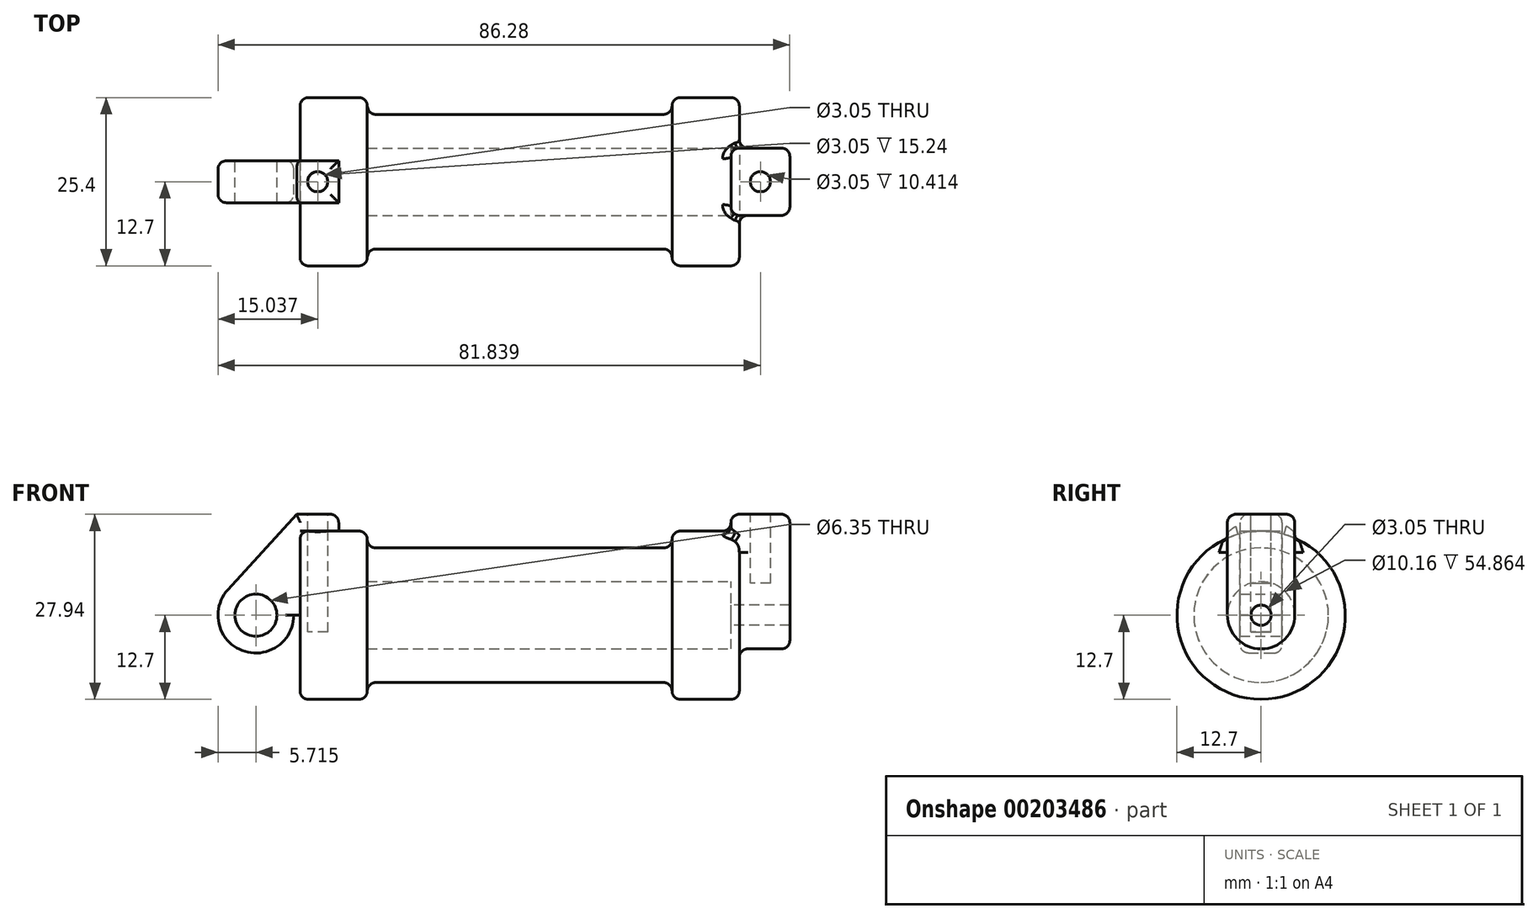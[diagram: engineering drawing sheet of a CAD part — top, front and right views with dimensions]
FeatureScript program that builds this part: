
annotation { "Feature Type Name" : "Feature", "Feature Type Description" : "" }
export const myFeature = defineFeature(function(context is Context, id is Id, definition is map)
    precondition{}
    {
        {
            var Q0;
            Q0=qCreatedBy(makeId("Front.planeOp"),FACE);
            var sketch = newSketch(context, id + "F0", { "sketchPlane" : qUnion([Q0])});
            skLineSegment(sketch, "E0", {"start": v(0, 0) * mm, "end": v(0, 12.7) * mm});
            skLineSegment(sketch, "E1", {"start": v(0, 12.7) * mm, "end": v(10.16, 12.7) * mm});
            skLineSegment(sketch, "E2", {"start": v(10.16, 12.7) * mm, "end": v(10.16, 10.16) * mm});
            skLineSegment(sketch, "E3", {"start": v(10.16, 10.16) * mm, "end": v(56.13, 10.16) * mm});
            skLineSegment(sketch, "E4", {"start": v(56.13, 10.16) * mm, "end": v(56.13, 12.7) * mm});
            skLineSegment(sketch, "E5", {"start": v(56.13, 12.7) * mm, "end": v(66.3, 12.7) * mm});
            skLineSegment(sketch, "E6", {"start": v(66.3, 12.7) * mm, "end": v(66.3, 0) * mm});
            skLineSegment(sketch, "E7", {"start": v(66.3, 0) * mm, "end": v(0, 0) * mm});
            skLineSegment(sketch, "E8", {"start": v(5.84, 15.24) * mm, "end": v(-0.5, 15.24) * mm});
            skLineSegment(sketch, "E9", {"start": v(-0.5, 15.24) * mm, "end": v(-10.88, 3.85) * mm});
            skLineSegment(sketch, "E10", {"start": v(0, 0) * mm, "end": v(-6.65, 0) * mm});
            skCircle(sketch, "E11", {"center": v(-6.65, 0) * mm, "radius": 5.72 * mm});
            skCircle(sketch, "E12", {"center": v(-6.65, 0) * mm, "radius": 3.18 * mm});
            skLineSegment(sketch, "E13", {"start": v(5.84, 15.24) * mm, "end": v(5.84, -9.4) * mm});
            skLineSegment(sketch, "E14", {"start": v(5.84, -9.4) * mm, "end": v(-8.18, -5.5) * mm});
            skSolve(sketch);
        }
        {
            var Q0;
            {var subQ0=sQuery(id+"F0.wireOp",EDGE,"E0");Q0=makeQuery(id+"F0.imprint","IMPRINT",FACE,{"disambiguationData":[TD([[makeQuery(id+"F0.imprint","IMPRINT",EDGE,{"derivedFrom":subQ0}),-1.0]])]});}
            var Q1;
            {var subQ0=sQuery(id+"F0.wireOp",EDGE,"E2");Q1=makeQuery(id+"F0.imprint","IMPRINT",FACE,{"disambiguationData":[TD([[makeQuery(id+"F0.imprint","IMPRINT",EDGE,{"derivedFrom":subQ0}),-1.0]])]});}
            var Q2;
            Q2=sQuery(id+"F0.wireOp",EDGE,"E7");
            revolve(context, id + "F1", {"entities" : qUnion([Q0, Q1]), "axis" : qUnion([Q2]), "revolveType" : RevolveType.FULL});
        }
        {
            var Q0;
            {var subQ3=sQuery(id+"F0.wireOp",EDGE,"E0");Q0=makeQuery(id+"F0.imprint","IMPRINT",FACE,{"disambiguationData":[TD([[makeQuery(id+"F0.imprint","IMPRINT",EDGE,{"derivedFrom":subQ3}),1.0]])]});}
            var Q1;
            {var subQ4=sQuery(id+"F0.wireOp",EDGE,"E12");Q1=makeQuery(id+"F0.imprint","IMPRINT",FACE,{"disambiguationData":[TD([[makeQuery(id+"F0.imprint","IMPRINT",EDGE,{"derivedFrom":subQ4}),-1.0]])]});}
            extrude(context, id + "F2", {"entities" : qUnion([Q0, Q1]), "endBound" : BoundingType.SYMMETRIC, "depth" : 6.35 * mm});
        }
        {
            var Q0;
            Q0=makeQuery(id+"F1.opRevolve","SWEPT_FACE",FACE,{"disambiguationData":[OSD([sQuery(id+"F0.wireOp",EDGE,"E6")])]});
            var sketch = newSketch(context, id + "F3", { "sketchPlane" : qUnion([Q0])});
            skCircle(sketch, "E15", {"center": v(0, 0) * mm, "radius": 1.52 * mm});
            skCircle(sketch, "E16", {"center": v(0, 0) * mm, "radius": 5.08 * mm});
            skLineSegment(sketch, "E17", {"start": v(5.08, 0) * mm, "end": v(5.08, 15.24) * mm});
            skLineSegment(sketch, "E18.MirrorCS", {"start": v(-5.08, 0) * mm, "end": v(-5.08, 15.24) * mm});
            skLineSegment(sketch, "E19", {"start": v(-5.08, 15.24) * mm, "end": v(5.08, 15.24) * mm});
            skSolve(sketch);
        }
        {
            var Q0;
            Q0=makeQuery(id+"F3.imprint","IMPRINT",FACE,{"disambiguationData":[TD([[makeQuery(id+"F3.imprint","IMPRINT",EDGE,{"derivedFrom":sQuery(id+"F3.wireOp",EDGE,"E15")}),-1.0]])]});
            var Q1;
            Q1=makeQuery(id+"F3.imprint","IMPRINT",FACE,{"disambiguationData":[TD([[makeQuery(id+"F3.imprint","IMPRINT",EDGE,{"derivedFrom":sQuery(id+"F3.wireOp",EDGE,"E15")}),1.0]])]});
            extrude(context, id + "F4", {"entities" : qUnion([Q0, Q1]), "operationType" : NewBodyOperationType.REMOVE, "oppositeDirection" : true, "depth" : 56.13 * mm});
        }
        {
            var Q0;
            {var subQ0=sQuery(id+"F3.wireOp",EDGE,"E19");Q0=makeQuery(id+"F3.imprint","IMPRINT",FACE,{"disambiguationData":[TD([[makeQuery(id+"F3.imprint","IMPRINT",EDGE,{"derivedFrom":subQ0}),-1.0]])]});}
            var Q1;
            {var subQ0=sQuery(id+"F3.wireOp",EDGE,"E17");var subQ1=sQuery(id+"F3.wireOp",EDGE,"E16");var subQ2=makeQuery(id+"F3.imprint","INTERSECT",VERTEX,{"derivedFrom":[subQ1,subQ0]});Q1=makeQuery(id+"F3.imprint","IMPRINT",FACE,{"disambiguationData":[TD([[makeQuery(id+"F3.imprint","IMPRINT",EDGE,{"disambiguationData":[TD([[subQ2,-1.0]])],"derivedFrom":subQ1}),-1.0]])]});}
            var Q2;
            Q2=makeQuery(id+"F3.imprint","IMPRINT",FACE,{"disambiguationData":[TD([[makeQuery(id+"F3.imprint","IMPRINT",EDGE,{"derivedFrom":sQuery(id+"F3.wireOp",EDGE,"E15")}),-1.0]])]});
            extrude(context, id + "F5", {"entities" : qUnion([Q0, Q1, Q2]), "operationType" : NewBodyOperationType.ADD, "depth" : 7.62 * mm, "hasSecondDirection" : true, "secondDirectionOppositeDirection" : true, "secondDirectionDepth" : 1.27 * mm});
        }
        {
            var Q0;
            Q0=makeQuery(id+"F5.opExtrude","SWEPT_FACE",FACE,{"disambiguationData":[OSD([sQuery(id+"F3.wireOp",EDGE,"E19")])]});
            var sketch = newSketch(context, id + "F6", { "sketchPlane" : qUnion([Q0])});
            skCircle(sketch, "E20", {"center": v(69.47, 0) * mm, "radius": 1.52 * mm});
            skSolve(sketch);
        }
        {
            var Q0;
            Q0=makeQuery(id+"F2.opExtrude","SWEPT_FACE",FACE,{"disambiguationData":[OSD([sQuery(id+"F0.wireOp",EDGE,"E8")])]});
            var sketch = newSketch(context, id + "F7", { "sketchPlane" : qUnion([Q0])});
            skCircle(sketch, "E21", {"center": v(2.67, 0) * mm, "radius": 1.52 * mm});
            skSolve(sketch);
        }
        {
            var Q0;
            Q0=makeQuery(id+"F7.imprint","IMPRINT",FACE,{"disambiguationData":[TD([[makeQuery(id+"F7.imprint","IMPRINT",EDGE,{"derivedFrom":sQuery(id+"F7.wireOp",EDGE,"E21")}),1.0]])]});
            extrude(context, id + "F8", {"entities" : qUnion([Q0]), "operationType" : NewBodyOperationType.REMOVE, "oppositeDirection" : true, "depth" : 17.78 * mm});
        }
        {
            var Q0;
            Q0=makeQuery(id+"F6.imprint","IMPRINT",FACE,{"disambiguationData":[TD([[makeQuery(id+"F6.imprint","IMPRINT",EDGE,{"derivedFrom":sQuery(id+"F6.wireOp",EDGE,"E20")}),1.0]])]});
            extrude(context, id + "F9", {"entities" : qUnion([Q0]), "operationType" : NewBodyOperationType.REMOVE, "oppositeDirection" : true, "depth" : 10.4 * mm});
        }
        {
            var Q0;
            Q0=makeQuery(id+"F1.opRevolve","SWEPT_EDGE",EDGE,{"disambiguationData":[OSD([sQuery(id+"F0.wireOp",EDGE,"E1"),sQuery(id+"F0.wireOp",EDGE,"E2")])]});
            var Q1;
            Q1=makeQuery(id+"F1.opRevolve","SWEPT_EDGE",EDGE,{"disambiguationData":[OSD([sQuery(id+"F0.wireOp",EDGE,"E2"),sQuery(id+"F0.wireOp",EDGE,"E3")])]});
            var Q2;
            Q2=makeQuery(id+"F1.opRevolve","SWEPT_EDGE",EDGE,{"disambiguationData":[OSD([sQuery(id+"F0.wireOp",EDGE,"E0"),sQuery(id+"F0.wireOp",EDGE,"E1")])]});
            var Q3;
            Q3=makeQuery(id+"F1.opRevolve","SWEPT_EDGE",EDGE,{"disambiguationData":[OSD([sQuery(id+"F0.wireOp",EDGE,"E5"),sQuery(id+"F0.wireOp",EDGE,"E6")])]});
            var Q4;
            Q4=makeQuery(id+"F1.opRevolve","SWEPT_EDGE",EDGE,{"disambiguationData":[OSD([sQuery(id+"F0.wireOp",EDGE,"E4"),sQuery(id+"F0.wireOp",EDGE,"E5")])]});
            var Q5;
            Q5=makeQuery(id+"F1.opRevolve","SWEPT_EDGE",EDGE,{"disambiguationData":[OSD([sQuery(id+"F0.wireOp",EDGE,"E3"),sQuery(id+"F0.wireOp",EDGE,"E4")])]});
            fillet(context, id + "F10", {"entities" : qUnion([Q0, Q1, Q2, Q3, Q4, Q5]), "radius" : 1.27 * mm, "tangentPropagation" : true, "allowEdgeOverflow" : false});
        }
        {
            var Q0;
            Q0=makeQuery(id+"F2.opExtrude","CAP_EDGE",EDGE,{"disambiguationData":[OSD([sQuery(id+"F0.wireOp",EDGE,"E8")])],"isStart":false});
            var Q1;
            Q1=makeQuery(id+"F2.opExtrude","SWEPT_EDGE",EDGE,{"disambiguationData":[OSD([sQuery(id+"F0.wireOp",EDGE,"E8"),sQuery(id+"F0.wireOp",EDGE,"E13")])]});
            var Q2;
            Q2=makeQuery(id+"F2.opExtrude","CAP_EDGE",EDGE,{"disambiguationData":[OSD([sQuery(id+"F0.wireOp",EDGE,"E8")])],"isStart":true});
            var Q3;
            Q3=makeQuery(id+"F2.opExtrude","CAP_EDGE",EDGE,{"disambiguationData":[OSD([sQuery(id+"F0.wireOp",EDGE,"E9")])],"isStart":false});
            var Q4;
            Q4=makeQuery(id+"F2.opExtrude","CAP_EDGE",EDGE,{"disambiguationData":[OSD([sQuery(id+"F0.wireOp",EDGE,"E9")])],"isStart":true});
            fillet(context, id + "F11", {"entities" : qUnion([Q0, Q1, Q2, Q3, Q4]), "radius" : 1.27 * mm, "tangentPropagation" : true, "allowEdgeOverflow" : false});
        }
        {
            var Q0;
            Q0=makeQuery(id+"F5.boolean.opBoolean","INTERSECT",EDGE,{"derivedFrom":[makeQuery(id+"F1.opRevolve","SWEPT_FACE",FACE,{"disambiguationData":[OSD([sQuery(id+"F0.wireOp",EDGE,"E5")])]}),makeQuery(id+"F5.opExtrude","CAP_FACE",FACE,{"disambiguationData":[OSD([sQuery(id+"F3.wireOp",EDGE,"E15"),sQuery(id+"F3.wireOp",EDGE,"E16"),sQuery(id+"F3.wireOp",EDGE,"E17"),sQuery(id+"F3.wireOp",EDGE,"E18.MirrorCS"),sQuery(id+"F3.wireOp",EDGE,"E19")])],"isStart":true})]});
            var Q1;
            Q1=makeQuery(id+"F10.opFillet","BLEND_EDGE",EDGE,{"blendedFrom":[makeQuery(id+"F1.opRevolve","SWEPT_EDGE",EDGE,{"disambiguationData":[OSD([sQuery(id+"F0.wireOp",EDGE,"E5"),sQuery(id+"F0.wireOp",EDGE,"E6")])]}),makeQuery(id+"F5.opExtrude","SWEPT_FACE",FACE,{"disambiguationData":[OSD([sQuery(id+"F3.wireOp",EDGE,"E18.MirrorCS")])]})],"blendedInto":[makeQuery(id+"F5.opExtrude","SWEPT_FACE",FACE,{"disambiguationData":[OSD([sQuery(id+"F3.wireOp",EDGE,"E18.MirrorCS")])]})]});
            var Q2;
            Q2=makeQuery(id+"F5.opExtrude","CAP_EDGE",EDGE,{"disambiguationData":[OSD([sQuery(id+"F3.wireOp",EDGE,"E18.MirrorCS")])],"isStart":true});
            var Q3;
            Q3=makeQuery(id+"F5.opExtrude","SWEPT_EDGE",EDGE,{"disambiguationData":[OSD([sQuery(id+"F3.wireOp",EDGE,"E18.MirrorCS"),sQuery(id+"F3.wireOp",EDGE,"E19")])]});
            var Q4;
            Q4=makeQuery(id+"F5.opExtrude","CAP_EDGE",EDGE,{"disambiguationData":[OSD([sQuery(id+"F3.wireOp",EDGE,"E19")])],"isStart":true});
            var Q5;
            Q5=makeQuery(id+"F5.opExtrude","CAP_EDGE",EDGE,{"disambiguationData":[OSD([sQuery(id+"F3.wireOp",EDGE,"E18.MirrorCS")])],"isStart":false});
            var Q6;
            Q6=makeQuery(id+"F5.opExtrude","CAP_EDGE",EDGE,{"disambiguationData":[OSD([sQuery(id+"F3.wireOp",EDGE,"E19")])],"isStart":false});
            var Q7;
            Q7=makeQuery(id+"F5.opExtrude","SWEPT_EDGE",EDGE,{"disambiguationData":[OSD([sQuery(id+"F3.wireOp",EDGE,"E17"),sQuery(id+"F3.wireOp",EDGE,"E19")])]});
            var Q8;
            Q8=makeQuery(id+"F5.opExtrude","CAP_EDGE",EDGE,{"disambiguationData":[OSD([sQuery(id+"F3.wireOp",EDGE,"E17")])],"isStart":true});
            fillet(context, id + "F12", {"entities" : qUnion([Q0, Q1, Q2, Q3, Q4, Q5, Q6, Q7, Q8]), "radius" : 1.27 * mm, "tangentPropagation" : true, "allowEdgeOverflow" : false});
        }
    });
